# Revit family: Värmelampa Exclusive 22001
name_source: partatom
category: Lighting Fixtures
units: mm (PartAtom-declared; Revit-internal decimal feet)

## family parameters
Always vertical = Yes
Cut with Voids When Loaded = No
Host = Ceiling
Light Source = No
OmniClass Number = 23.80.70.11
OmniClass Title = Luminaries for Internal Lighting
Part Type = Normal
Room Calculation Point = No
Round Connector Dimension = Use Diameter
Shared = No

## types (4) — shared parameters
Lamp Hanger Material = AMA - Glossy Black Dark
zero-valued in all types: Default Elevation

## per-type parameters (varying)
| type | Lamp Type |
| 22001-S | Värmelampa Classic M 22001 : 22001-S |
| 22001-M | Värmelampa Classic M 22001 : 22001-M |
| 22001-Ko | Värmelampa Classic M 22001 : 22001-Ko |
| 22001-C | Värmelampa Classic M 22001 : 22001-C |

note: column(s) folded — value = type name in every type: Artikelnummer

## geometry (parser evidence)
native form markers: Sweep x5
no freeform markers — native parametric forms only
